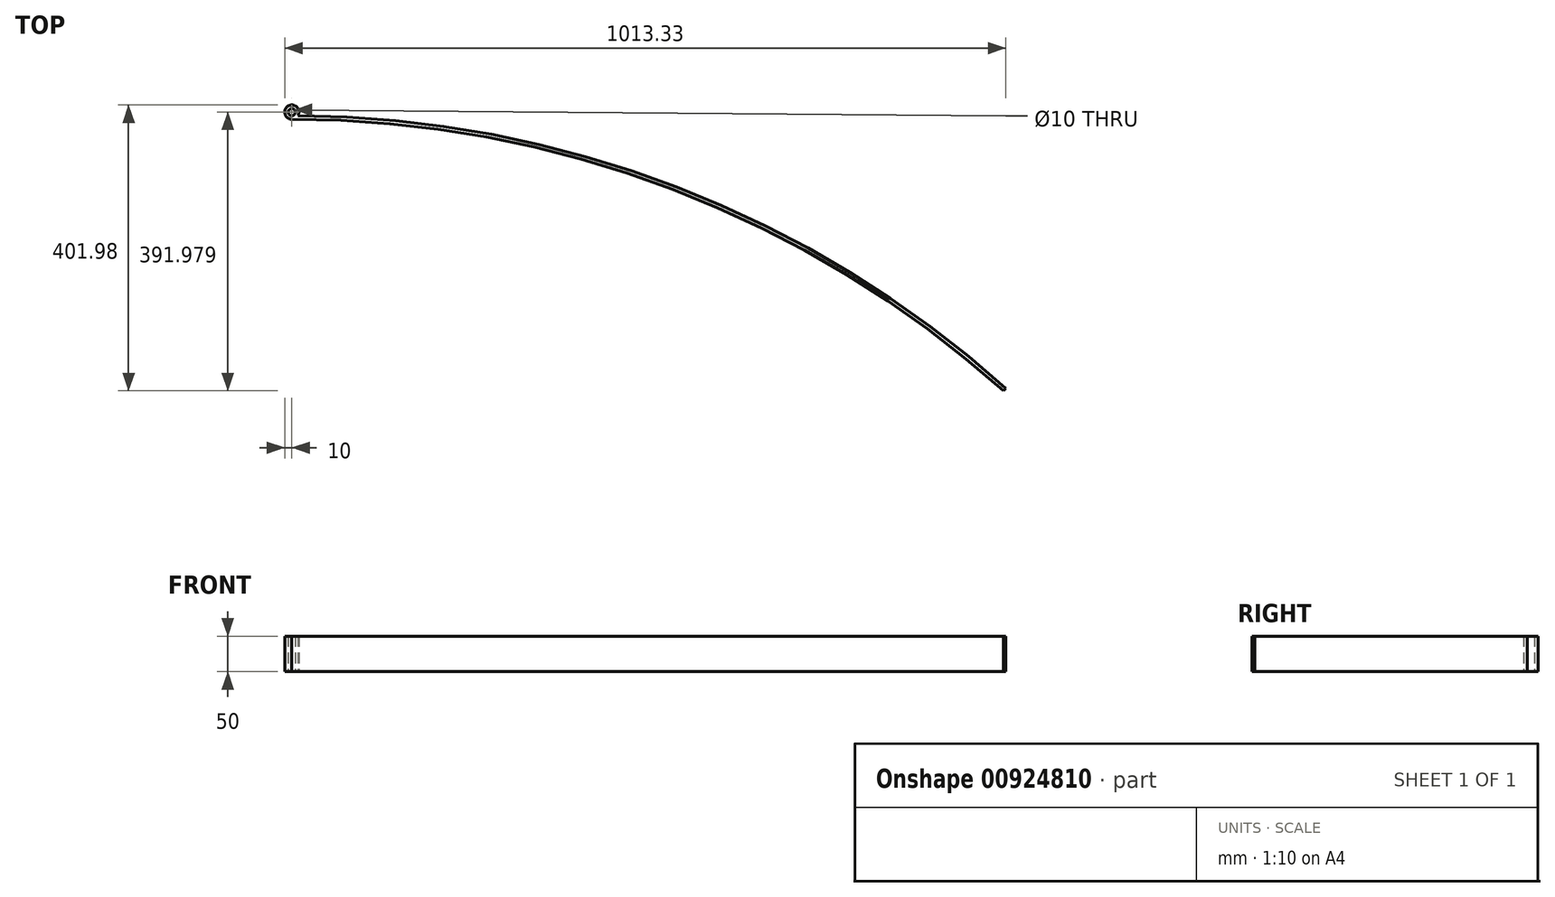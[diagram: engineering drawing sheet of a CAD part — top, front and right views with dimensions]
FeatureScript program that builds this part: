
annotation { "Feature Type Name" : "Feature", "Feature Type Description" : "" }
export const myFeature = defineFeature(function(context is Context, id is Id, definition is map)
    precondition{}
    {
        {
            var Q0;
            Q0=qCreatedBy(makeId("Top.planeOp"),FACE);
            var sketch = newSketch(context, id + "F0", { "sketchPlane" : qUnion([Q0])});
            skArc(sketch, "E0", {"start": v(1000, 1118.03) * mm, "mid": v(535.23, 1401.26) * mm, "end": v(0, 1500) * mm});
            skArc(sketch, "E1.0", {"start": v(1003.33, 1121.76) * mm, "mid": v(537.02, 1405.93) * mm, "end": v(0, 1505) * mm});
            skCircle(sketch, "E2", {"center": v(0, 1510) * mm, "radius": 10 * mm});
            skCircle(sketch, "E3.0", {"center": v(0, 1510) * mm, "radius": 5 * mm});
            skLineSegment(sketch, "E4", {"start": v(0, 1505) * mm, "end": v(0, 1500) * mm});
            skLineSegment(sketch, "E5", {"start": v(1000, 1118.03) * mm, "end": v(1003.33, 1121.76) * mm});
            skArc(sketch, "E6", {"start": v(1015.92, 226.94) * mm, "mid": v(366.27, 590.3) * mm, "end": v(-283.37, 226.94) * mm});
            skArc(sketch, "E7", {"start": v(-223.73, 190.3) * mm, "mid": v(366.27, 520.3) * mm, "end": v(956.27, 190.3) * mm});
            skLineSegment(sketch, "E8", {"start": v(956.27, 190.3) * mm, "end": v(1015.92, 226.94) * mm});
            skLineSegment(sketch, "E9", {"start": v(-223.73, 190.3) * mm, "end": v(-283.37, 226.94) * mm});
            skLineSegment(sketch, "E10", {"start": v(366.27, 190.3) * mm, "end": v(956.27, 190.3) * mm});
            skLineSegment(sketch, "E11", {"start": v(366.27, 190.3) * mm, "end": v(366.27, 520.3) * mm});
            skLineSegment(sketch, "E12", {"start": v(366.27, 190.3) * mm, "end": v(-223.73, 190.3) * mm});
            skSolve(sketch);
        }
        {
            var Q0;
            {var subQ0=sQuery(id+"F0.wireOp",EDGE,"E4");var subQ1=sQuery(id+"F0.wireOp",EDGE,"E1.0");var subQ2=makeQuery(id+"F0.imprint","INTERSECT",VERTEX,{"derivedFrom":[subQ1,subQ0]});Q0=makeQuery(id+"F0.imprint","IMPRINT",FACE,{"disambiguationData":[TD([[makeQuery(id+"F0.imprint","IMPRINT",EDGE,{"disambiguationData":[TD([[subQ2,1.0]])],"derivedFrom":subQ1}),1.0]])]});}
            var Q1;
            Q1=makeQuery(id+"F0.imprint","IMPRINT",FACE,{"disambiguationData":[TD([[makeQuery(id+"F0.imprint","IMPRINT",EDGE,{"derivedFrom":sQuery(id+"F0.wireOp",EDGE,"E3.0")}),-1.0]])]});
            var Q2;
            {var subQ1=sQuery(id+"F0.wireOp",EDGE,"E0");Q2=makeQuery(id+"F0.imprint","IMPRINT",FACE,{"disambiguationData":[TD([[makeQuery(id+"F0.imprint","IMPRINT",EDGE,{"derivedFrom":subQ1}),-1.0]])]});}
            extrude(context, id + "F1", {"entities" : qUnion([Q0, Q1, Q2]), "depth" : 50 * mm, "offsetDistance" : 25 * mm});
        }
    });
